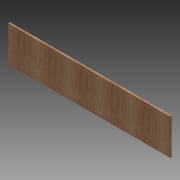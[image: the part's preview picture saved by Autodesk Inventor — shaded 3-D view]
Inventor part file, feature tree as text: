
AUTODESK INVENTOR PART (.ipt)
format: ipt  version: 2013 (Build 170138000, 138)  size: 80,896 bytes
history: native  units: in
note: dims shown in document units (in); Inventor stores cm internally (conversion verified against a paired STEP export)
features: extrude x1, sketch x1
ambient origin geometry x8: Origin, YZ Plane, XZ Plane, XY Plane, X Axis, Y Axis, Z Axis, Center Point
bodies: Solid1 (feature_tree)
feature tree (2):
  extrude  "Extrusion1"  Depth=52.0in
  sketch  "Sketch1"  dims[d0=11.5in d1=52.0in d2=0.5in d3=0.0in]
